# Revit family: FOCUS-R90
name_source: partatom
category: Осветительные приборы
revit_build: Autodesk Revit 2017 (Build: 20160225_1515(x64)
units: mm (PartAtom-declared; Revit-internal decimal feet)

## family parameters
Всегда вертикально = Да
Источник света = Да
На основе рабочей плоскости = Нет
Общий = Нет
При загрузке вырезать с полостями = Нет
Размер круглого соединителя = Использовать диаметр
Тип детали = Нормальный
Точка расчета площади = Нет

## types (5) — shared parameters
ADSK_Единица измерения = шт.
ADSK_Завод-изготовитель = ARLIGHT
ADSK_Классификация нагрузок = Освещение
ADSK_Количество фаз = 1
ADSK_Количество фаз числовое = 1
ADSK_Коэффициент мощности = 0.5
ADSK_Масса_Текст = 0.81
ADSK_Наименование = Светильник
ADSK_Напряжение = 230 В
ADSK_Номинальная мощность = 9 Вт
ADSK_Полная мощность = 18 В·А
ADSK_Размер_Высота = 126 мм
ADSK_Размер_Диаметр = 90 мм
ADSK_Ток = 0 А
ARL_Драйвер = Встроенный (DC 200mA 20-40V)
ARL_Индекс цветопередачи = >80
ARL_Класс защиты от поражения электрическим током = II
ARL_Класс пылевлагозащиты = IP20
ARL_Область использования = Для основного, декоративного и акцентного освещения в жилых, офисных, торговых, выставочных и других помещениях
ARL_Рабочая температура окружающей среды = -10...+50 °C
ARL_Серия = FOCUS
FOCUS
ARL_Способ монтажа = Накладной
ARL_Тип товара = Светильник
ARL_Угол обзора = 24°
URL = https://arlight.ru
Видимая форма излучения при визуализации = Нет
Группа модели = Светильники
Изготовитель = ARLIGHT
Изготовитель (сайт) = www.arlight.ru
Изготовитель (телефон) = 8 800 505 26 29
Полная установленная мощность = 18 В·А
Разработчик = НТЦ Конструктор
Разработчик (URL) = https://constructor.ru
Разработчик (телефон) = +7 (495) 781-05-35
Светофильтр = 16777215
Смещение цветовой температуры при затухании лампы = <Нет>
Угол наклона = 90.00°

## per-type parameters (varying)
| type | ADSK_Код изделия | ADSK_Марка | ARL_Материал корпуса | ARL_Обозначение корпуса | ARL_Цвет покрытия | ARL_Цвет свечения | Излучение по диаметру окружности | Комментарии к типоразмеру | Описание | Файл фотометрической сетки |
| 021425 Светильник SP-FOCUS-R90-9W White | Арт. 021425 | SP-FOCUS-R90-9W White | Металл, белый | Корпус цилиндр, металл, цвет белый | Белый | Белый 6000K | 50 мм | Арт. 021425 | Накладной светильник 9 Вт, белый корпус цилиндр. Цвет БЕЛЫЙ 6000K, св.поток 720-810лм, CRI(Ra)>80, наклоняемая ось, угол 24°. Размер Ф90x126 мм. Питание AC 180-240V, 9 Вт, встроенный драйвер (DC 200mA 20-40V). | 021425_SP-FOCUS-R90-9W White.ies |
| 021424 Светильник SP-FOCUS-R90-9W Day White | Арт. 021424 | SP-FOCUS-R90-9W Day White | Металл, белый | Корпус цилиндр, металл, цвет белый | Белый | Дневной 4000K | 45 мм | Арт. 021424 | Накладной светильник 9 Вт, белый корпус цилиндр. Цвет ДНЕВНОЙ БЕЛЫЙ 4000K, св.поток 720-810лм, CRI(Ra)>80, наклоняемая ось, угол 24°. Размер Ф90x126 мм. Питание AC 180-240V, 9 Вт, встроенный драйвер. | 021424_SP-FOCUS-R90-9W Day White 4000.ies |
| 021064 Светильник SP-FOCUS-R90-9W Warm White | Арт. 021064 | SP-FOCUS-R90-9W Warm White | Металл, белый | Корпус цилиндр, металл, цвет белый | Белый | Теплый 3000K | 45 мм | Арт. 021064 | Накладной светильник 9 Вт, белый корпус цилиндр. Цвет ТЕПЛЫЙ БЕЛЫЙ 3000K, св.поток 720-810лм, CRI(Ra)>80, наклоняемая ось, угол 24°. Размер Ф90x126 мм. Питание AC 180-240V, 9 Вт, встроенный драйвер (DC 200mA 20-40V). | 021064_SP-FOCUS-R90-9W Warm White 3000.ies |
| 029530 Светильник SP-FOCUS-R90-9W Day4000 (BK, 24 deg, 230V) | Арт. 029530 | SP-FOCUS-R90-9W Day4000 | Металл, чёрный | Корпус цилиндр, металл, цвет черный | Черный | Дневной 4000K | 45 мм | Арт. 029530 | Накладной светильник 9 Вт, черный корпус цилиндр. Цвет ДНЕВНОЙ 4000K, св.поток 720-810лм, CRI(Ra)>80, наклоняемая ось, угол 24°. Размер Ф90x126 мм. Питание AC 180-240V, 9 Вт, встроенный драйвер (DC 200mA 20-40V). | 029530_SP-FOCUS-R90-9W Day4000 (BK, 24 d, 230V).ies |
| 029531 Светильник SP-FOCUS-R90-9W Warm3000 (BK, 24 deg, 230V) | Арт. 029531 | SP-FOCUS-R90-9W Warm3000 | Металл, чёрный | Корпус цилиндр, металл, цвет черный | Черный | Теплый 3000K | 45 мм | Арт. 029531 | Накладной светильник 9 Вт, черный корпус цилиндр. Цвет ТЕПЛЫЙ 3000K, св.поток 720-810лм, CRI(Ra)>80, наклоняемая ось, угол 24°. Размер Ф90x126 мм. Питание AC 180-240V, 9 Вт, встроенный драйвер (DC 200mA 20-40V). | 029531_SP-FOCUS-R90-9W Warm3000 (BK, 24 d, 230V).ies |
